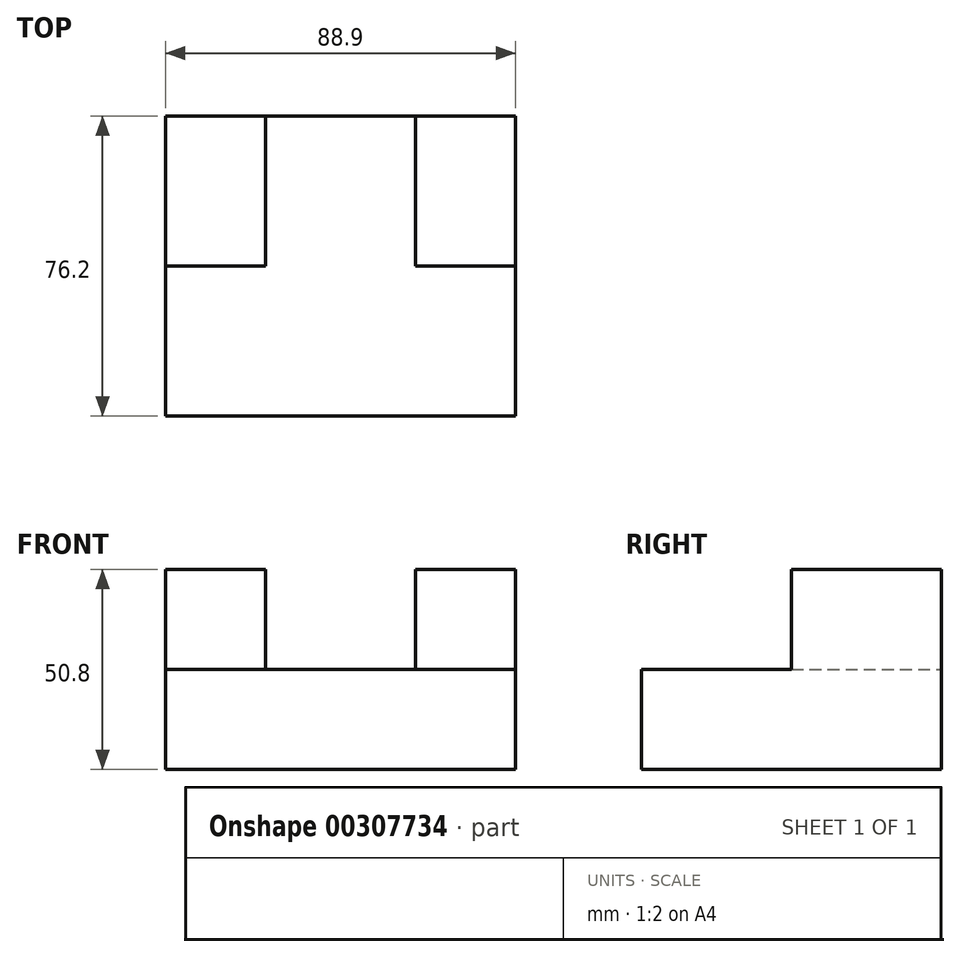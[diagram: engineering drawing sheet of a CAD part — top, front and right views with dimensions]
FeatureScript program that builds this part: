
annotation { "Feature Type Name" : "Feature", "Feature Type Description" : "" }
export const myFeature = defineFeature(function(context is Context, id is Id, definition is map)
    precondition{}
    {
        {
            var Q0;
            Q0=qCreatedBy(makeId("Top.planeOp"),FACE);
            var sketch = newSketch(context, id + "F0", { "sketchPlane" : qUnion([Q0])});
            skLineSegment(sketch, "E0", {"start": v(40.27, 34.63) * mm, "end": v(40.27, -41.57) * mm});
            skLineSegment(sketch, "E1", {"start": v(40.27, -41.57) * mm, "end": v(-48.63, -41.57) * mm});
            skLineSegment(sketch, "E2", {"start": v(-48.63, -41.57) * mm, "end": v(-48.63, 34.63) * mm});
            skLineSegment(sketch, "E3", {"start": v(-48.63, 34.63) * mm, "end": v(40.27, 34.63) * mm});
            skSolve(sketch);
        }
        {
            var Q0;
            Q0=makeQuery(id+"F0.imprint","IMPRINT",FACE,{"disambiguationData":[TD([[makeQuery(id+"F0.imprint","IMPRINT",EDGE,{"derivedFrom":sQuery(id+"F0.wireOp",EDGE,"E0")}),-1.0]])]});
            extrude(context, id + "F1", {"entities" : qUnion([Q0]), "depth" : 25.4 * mm});
        }
        {
            var Q0;
            Q0=makeQuery(id+"F1.opExtrude","CAP_FACE",FACE,{"disambiguationData":[OSD([sQuery(id+"F0.wireOp",EDGE,"E0"),sQuery(id+"F0.wireOp",EDGE,"E1"),sQuery(id+"F0.wireOp",EDGE,"E2"),sQuery(id+"F0.wireOp",EDGE,"E3")])],"isStart":false});
            var sketch = newSketch(context, id + "F2", { "sketchPlane" : qUnion([Q0])});
            skLineSegment(sketch, "E4", {"start": v(-48.63, 34.63) * mm, "end": v(-48.63, -3.47) * mm});
            skLineSegment(sketch, "E5", {"start": v(-48.63, -3.47) * mm, "end": v(-23.23, -3.47) * mm});
            skLineSegment(sketch, "E6", {"start": v(-23.23, -3.47) * mm, "end": v(-23.23, 34.63) * mm});
            skLineSegment(sketch, "E7", {"start": v(-23.23, 34.63) * mm, "end": v(-48.63, 34.63) * mm});
            skLineSegment(sketch, "E8", {"start": v(40.27, 34.63) * mm, "end": v(40.27, -3.47) * mm});
            skLineSegment(sketch, "E9", {"start": v(40.27, -3.47) * mm, "end": v(14.87, -3.47) * mm});
            skLineSegment(sketch, "E10", {"start": v(14.87, -3.47) * mm, "end": v(14.87, 34.63) * mm});
            skLineSegment(sketch, "E11", {"start": v(14.87, 34.63) * mm, "end": v(40.27, 34.63) * mm});
            skSolve(sketch);
        }
        {
            var Q0;
            Q0=makeQuery(id+"F2.imprint","IMPRINT",FACE,{"disambiguationData":[TD([[makeQuery(id+"F2.imprint","IMPRINT",EDGE,{"derivedFrom":sQuery(id+"F2.wireOp",EDGE,"E4")}),-1.0]])]});
            var Q1;
            Q1=makeQuery(id+"F2.imprint","IMPRINT",FACE,{"disambiguationData":[TD([[makeQuery(id+"F2.imprint","IMPRINT",EDGE,{"derivedFrom":sQuery(id+"F2.wireOp",EDGE,"E8")}),-1.0]])]});
            extrude(context, id + "F3", {"entities" : qUnion([Q0, Q1]), "operationType" : NewBodyOperationType.ADD, "depth" : 25.4 * mm});
        }
    });
